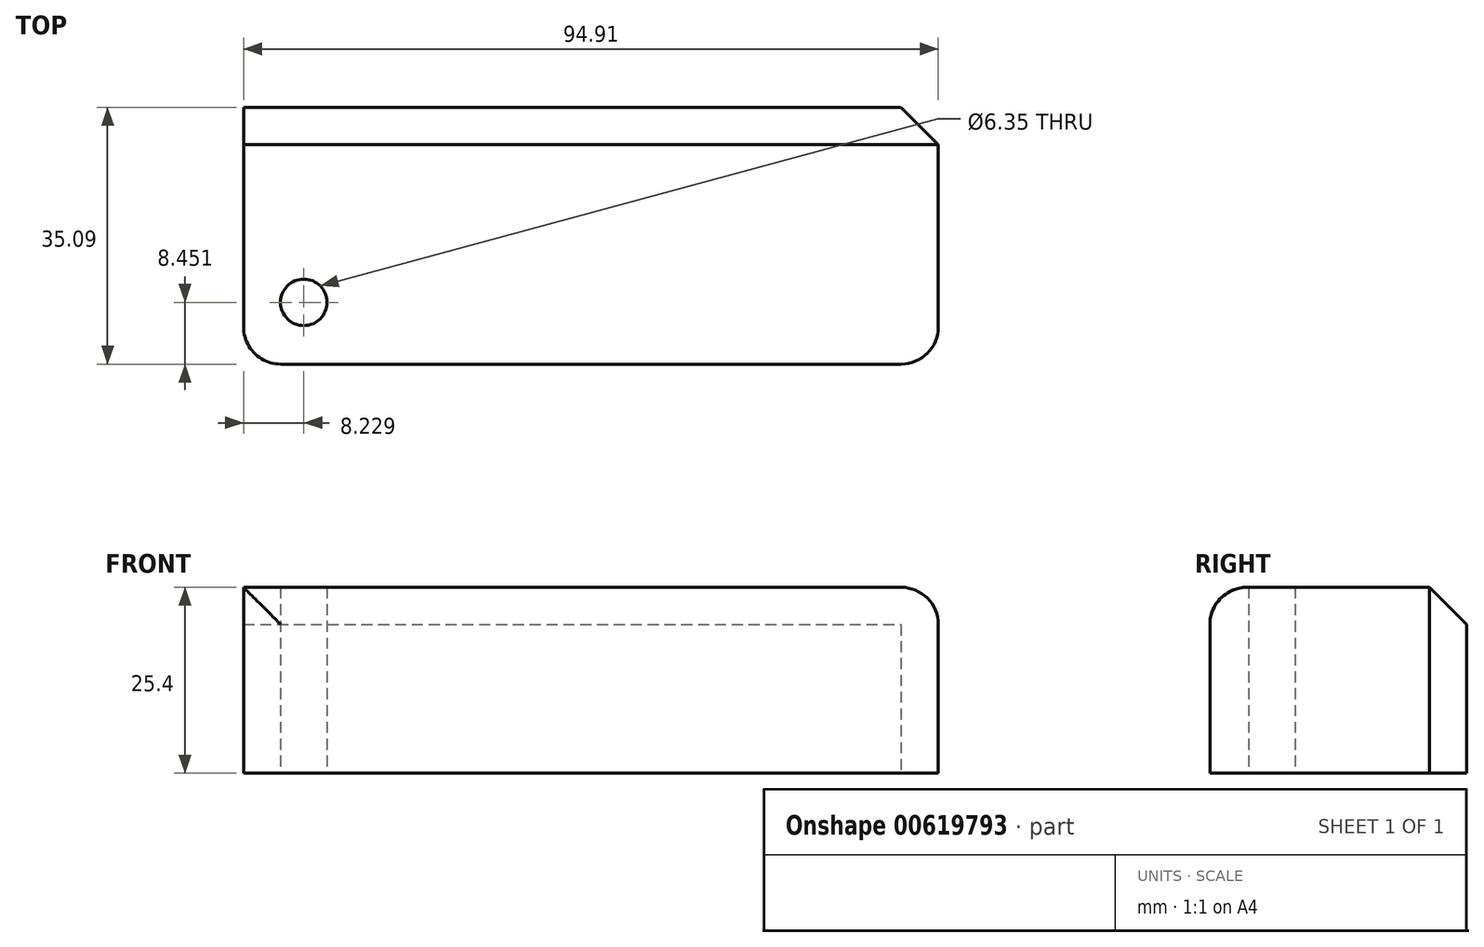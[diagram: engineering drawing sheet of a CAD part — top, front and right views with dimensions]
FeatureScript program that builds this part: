
annotation { "Feature Type Name" : "Feature", "Feature Type Description" : "" }
export const myFeature = defineFeature(function(context is Context, id is Id, definition is map)
    precondition{}
    {
        {
            var Q0;
            Q0=qCreatedBy(makeId("Top.planeOp"),FACE);
            var sketch = newSketch(context, id + "F0", { "sketchPlane" : qUnion([Q0])});
            skLineSegment(sketch, "E0.bottom", {"start": v(-88.04, 0) * mm, "end": v(6.87, 0) * mm});
            skLineSegment(sketch, "E0.top", {"start": v(-88.04, -35.09) * mm, "end": v(6.87, -35.09) * mm});
            skLineSegment(sketch, "E0.left", {"start": v(-88.04, 0) * mm, "end": v(-88.04, -35.09) * mm});
            skLineSegment(sketch, "E0.right", {"start": v(6.87, 0) * mm, "end": v(6.87, -35.09) * mm});
            skSolve(sketch);
        }
        {
            var Q0;
            Q0=makeQuery(id+"F0.imprint","IMPRINT",FACE,{"disambiguationData":[TD([[makeQuery(id+"F0.imprint","IMPRINT",EDGE,{"derivedFrom":sQuery(id+"F0.wireOp",EDGE,"E0.bottom")}),-1.0]])]});
            extrude(context, id + "F1", {"entities" : qUnion([Q0]), "depth" : 25.4 * mm, "offsetDistance" : 25.4 * mm});
        }
        {
            var Q0;
            Q0=makeQuery(id+"F1.opExtrude","CAP_EDGE",EDGE,{"disambiguationData":[OSD([sQuery(id+"F0.wireOp",EDGE,"E0.top")])],"isStart":false});
            var Q1;
            Q1=makeQuery(id+"F1.opExtrude","CAP_EDGE",EDGE,{"disambiguationData":[OSD([sQuery(id+"F0.wireOp",EDGE,"E0.right")])],"isStart":false});
            var Q2;
            Q2=makeQuery(id+"F1.opExtrude","SWEPT_EDGE",EDGE,{"disambiguationData":[OSD([sQuery(id+"F0.wireOp",EDGE,"E0.top"),sQuery(id+"F0.wireOp",EDGE,"E0.right")])]});
            var Q3;
            Q3=makeQuery(id+"F1.opExtrude","SWEPT_EDGE",EDGE,{"disambiguationData":[OSD([sQuery(id+"F0.wireOp",EDGE,"E0.top"),sQuery(id+"F0.wireOp",EDGE,"E0.left")])]});
            fillet(context, id + "F2", {"entities" : qUnion([Q0, Q1, Q2, Q3]), "radius" : 5.08 * mm, "tangentPropagation" : true, "allowEdgeOverflow" : false});
        }
        {
            var Q0;
            Q0=makeQuery(id+"F1.opExtrude","CAP_EDGE",EDGE,{"disambiguationData":[OSD([sQuery(id+"F0.wireOp",EDGE,"E0.bottom")])],"isStart":false});
            chamfer(context, id + "F3", {"entities" : qUnion([Q0]), "width" : 5.08 * mm, "tangentPropagation" : true});
        }
        {
            var Q0;
            Q0=makeQuery(id+"F1.opExtrude","CAP_FACE",FACE,{"disambiguationData":[OSD([sQuery(id+"F0.wireOp",EDGE,"E0.bottom"),sQuery(id+"F0.wireOp",EDGE,"E0.top"),sQuery(id+"F0.wireOp",EDGE,"E0.left"),sQuery(id+"F0.wireOp",EDGE,"E0.right")])],"isStart":true});
            var sketch = newSketch(context, id + "F4", { "sketchPlane" : qUnion([Q0])});
            skPoint(sketch, "E1", {"position": v(-79.81, 26.64) * mm});
            skSolve(sketch);
        }
        {
            var Q0;
            Q0=sQuery(id+"F4.wireOp",VERTEX,"E1");
            var Q1;
            Q1=makeQuery(id+"F1.opExtrude","SWEPT_BODY",BODY,{"disambiguationData":[OSD([sQuery(id+"F0.wireOp",EDGE,"E0.bottom"),sQuery(id+"F0.wireOp",EDGE,"E0.top"),sQuery(id+"F0.wireOp",EDGE,"E0.left"),sQuery(id+"F0.wireOp",EDGE,"E0.right")])]});
            hole(context, id + "F5", {"style" : HoleStyle.SIMPLE, "endStyle" : HoleEndStyle.THROUGH, "holeDiameter" : 6.35 * mm, "majorDiameter" : 6.35 * mm, "isTappedThrough" : true, "tappedDepth" : 12.7 * mm, "tapClearance" : 3, "locations" : qUnion([Q0]), "scope" : qUnion([Q1])});
        }
    });
